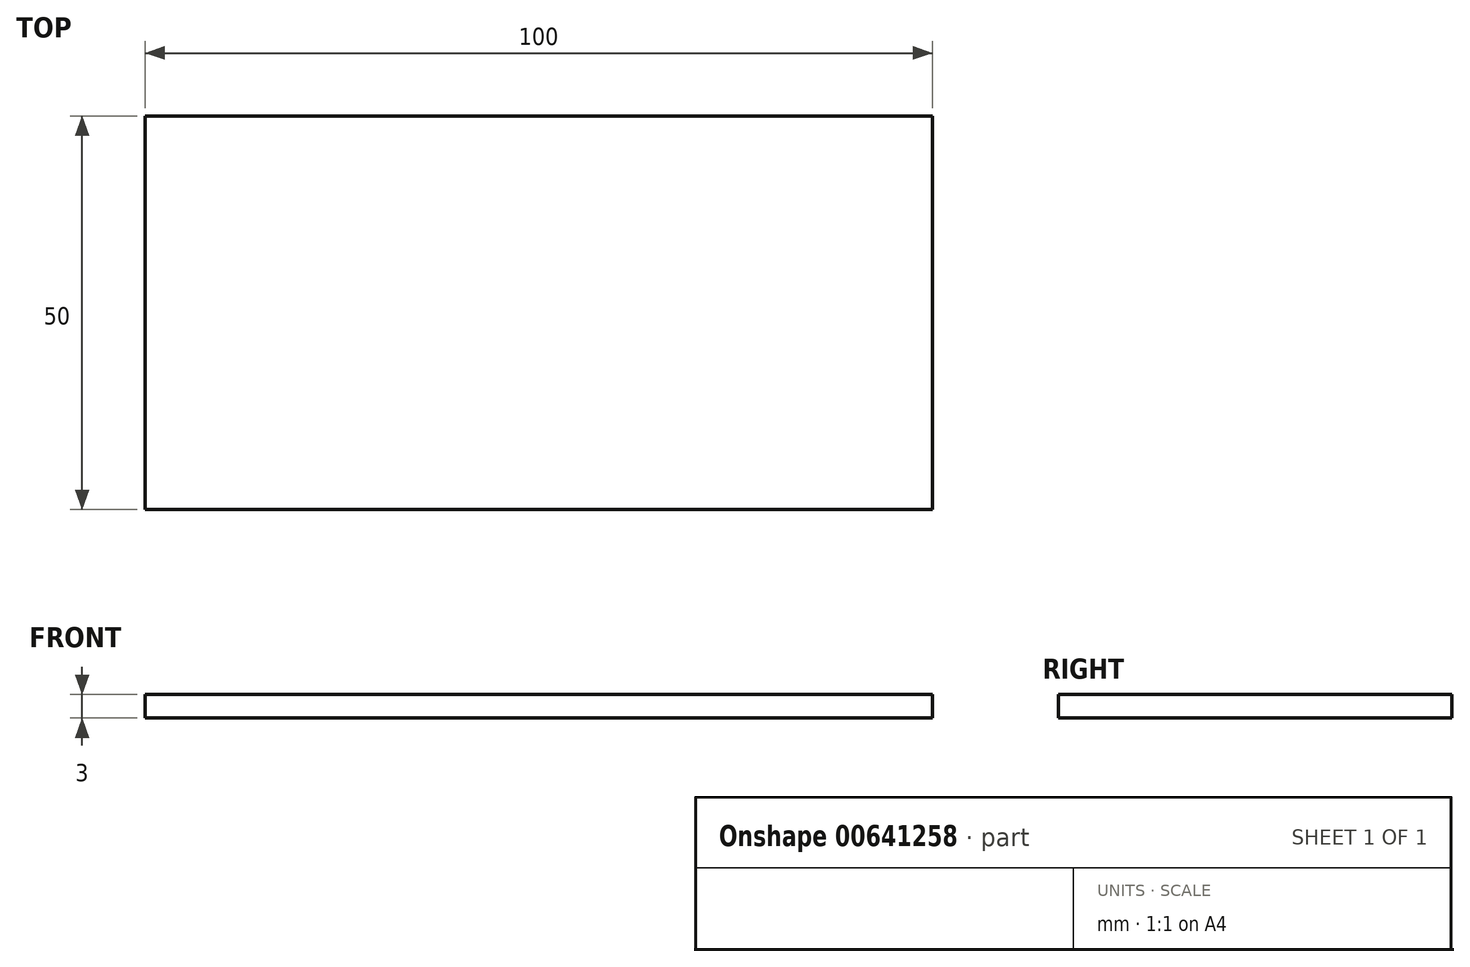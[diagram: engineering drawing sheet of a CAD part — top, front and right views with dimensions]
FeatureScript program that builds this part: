
annotation { "Feature Type Name" : "Feature", "Feature Type Description" : "" }
export const myFeature = defineFeature(function(context is Context, id is Id, definition is map)
    precondition{}
    {
        {
            var Q0;
            Q0=qCreatedBy(makeId("Top.planeOp"),FACE);
            var sketch = newSketch(context, id + "F0", { "sketchPlane" : qUnion([Q0])});
            skLineSegment(sketch, "E0.bottom", {"start": v(-52.31, 40.16) * mm, "end": v(47.69, 40.16) * mm});
            skLineSegment(sketch, "E0.top", {"start": v(-52.31, -9.84) * mm, "end": v(47.69, -9.84) * mm});
            skLineSegment(sketch, "E0.left", {"start": v(-52.31, 40.16) * mm, "end": v(-52.31, -9.84) * mm});
            skLineSegment(sketch, "E0.right", {"start": v(47.69, 40.16) * mm, "end": v(47.69, -9.84) * mm});
            skSolve(sketch);
        }
        {
            var Q0;
            Q0 = qSketchRegion(id + "F0", true);
            extrude(context, id + "F1", {"entities" : qUnion([Q0]), "depth" : 3 * mm, "offsetDistance" : 25 * mm});
        }
    });
